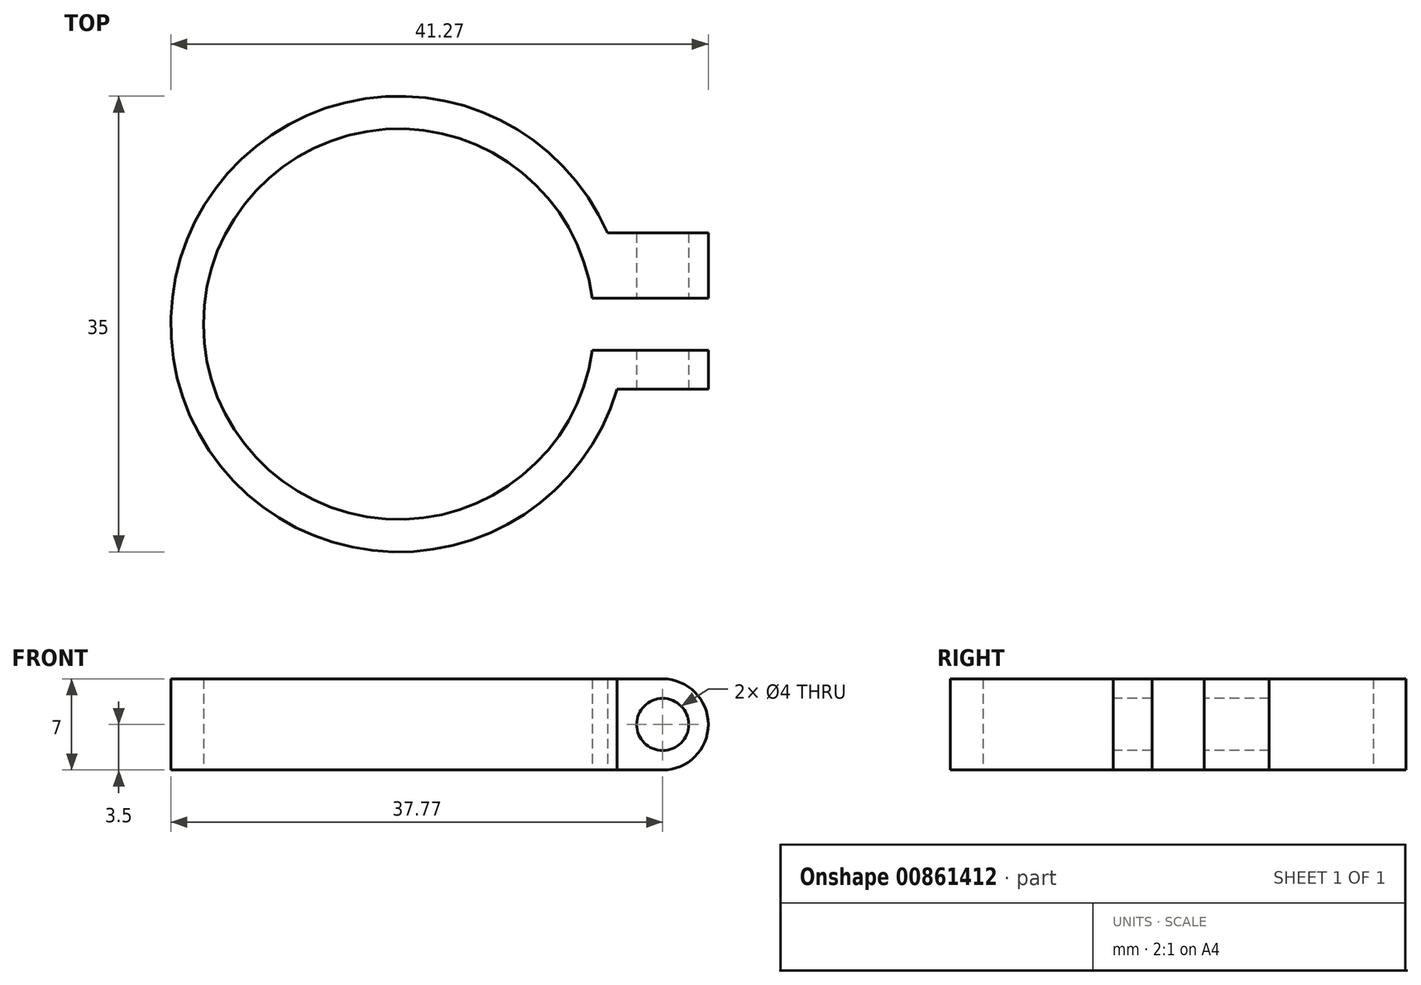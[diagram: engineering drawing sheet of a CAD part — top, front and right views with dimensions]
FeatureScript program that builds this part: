
annotation { "Feature Type Name" : "Feature", "Feature Type Description" : "" }
export const myFeature = defineFeature(function(context is Context, id is Id, definition is map)
    precondition{}
    {
        {
            var Q0;
            Q0=qCreatedBy(makeId("Top.planeOp"),FACE);
            var sketch = newSketch(context, id + "F0", { "sketchPlane" : qUnion([Q0])});
            skCircle(sketch, "E0", {"center": v(0, 0) * mm, "radius": 15 * mm});
            skCircle(sketch, "E1", {"center": v(0, 0) * mm, "radius": 17.5 * mm});
            skLineSegment(sketch, "E2", {"start": v(0, 0) * mm, "end": v(30.45, 0) * mm});
            skLineSegment(sketch, "E3.0", {"start": v(0, -2) * mm, "end": v(30.45, -2) * mm});
            skLineSegment(sketch, "E4.0", {"start": v(0, 2) * mm, "end": v(30.45, 2) * mm});
            skLineSegment(sketch, "E5.bottom", {"start": v(16.77, 5) * mm, "end": v(23.77, 5) * mm});
            skLineSegment(sketch, "E5.top", {"start": v(16.77, -5) * mm, "end": v(23.77, -5) * mm});
            skLineSegment(sketch, "E5.left", {"start": v(16.77, 5) * mm, "end": v(16.77, -5) * mm});
            skLineSegment(sketch, "E5.right", {"start": v(23.77, 5) * mm, "end": v(23.77, -5) * mm});
            skLineSegment(sketch, "E6.top", {"start": v(16.77, 7) * mm, "end": v(23.77, 7) * mm});
            skLineSegment(sketch, "E6.left", {"start": v(16.77, 5) * mm, "end": v(16.77, 7) * mm});
            skLineSegment(sketch, "E6.right", {"start": v(23.77, 5) * mm, "end": v(23.77, 7) * mm});
            skLineSegment(sketch, "E7.bottom", {"start": v(16.77, 5) * mm, "end": v(16.04, 5) * mm});
            skLineSegment(sketch, "E7.top", {"start": v(16.77, 7) * mm, "end": v(16.04, 7) * mm});
            skLineSegment(sketch, "E7.right", {"start": v(16.04, 5) * mm, "end": v(16.04, 7) * mm});
            skSolve(sketch);
        }
        {
            var Q0;
            {var subQ0=sQuery(id+"F0.wireOp",EDGE,"E4.0");var subQ1=sQuery(id+"F0.wireOp",EDGE,"E0");var subQ2=makeQuery(id+"F0.imprint","INTERSECT",VERTEX,{"derivedFrom":[subQ1,subQ0]});Q0=makeQuery(id+"F0.imprint","IMPRINT",FACE,{"disambiguationData":[TD([[makeQuery(id+"F0.imprint","IMPRINT",EDGE,{"disambiguationData":[TD([[subQ2,-1.0]])],"derivedFrom":subQ1}),-1.0]])]});}
            var Q1;
            {var subQ1=sQuery(id+"F0.wireOp",EDGE,"E1");var subQ3=sQuery(id+"F0.wireOp",EDGE,"E4.0");var subQ4=makeQuery(id+"F0.imprint","INTERSECT",VERTEX,{"derivedFrom":[subQ1,subQ3]});Q1=makeQuery(id+"F0.imprint","IMPRINT",FACE,{"disambiguationData":[TD([[makeQuery(id+"F0.imprint","IMPRINT",EDGE,{"disambiguationData":[TD([[subQ4,1.0]])],"derivedFrom":subQ3}),1.0]])]});}
            var Q2;
            {var subQ0=sQuery(id+"F0.wireOp",EDGE,"E5.bottom");Q2=makeQuery(id+"F0.imprint","IMPRINT",FACE,{"disambiguationData":[TD([[makeQuery(id+"F0.imprint","IMPRINT",EDGE,{"derivedFrom":subQ0}),-1.0]])]});}
            var Q3;
            {var subQ0=sQuery(id+"F0.wireOp",EDGE,"E5.top");Q3=makeQuery(id+"F0.imprint","IMPRINT",FACE,{"disambiguationData":[TD([[makeQuery(id+"F0.imprint","IMPRINT",EDGE,{"derivedFrom":subQ0}),1.0]])]});}
            var Q4;
            {var subQ1=sQuery(id+"F0.wireOp",EDGE,"E1");var subQ3=sQuery(id+"F0.wireOp",EDGE,"E3.0");var subQ4=makeQuery(id+"F0.imprint","INTERSECT",VERTEX,{"derivedFrom":[subQ1,subQ3]});Q4=makeQuery(id+"F0.imprint","IMPRINT",FACE,{"disambiguationData":[TD([[makeQuery(id+"F0.imprint","IMPRINT",EDGE,{"disambiguationData":[TD([[subQ4,1.0]])],"derivedFrom":subQ3}),-1.0]])]});}
            var Q5;
            {var subQ0=sQuery(id+"F0.wireOp",EDGE,"E5.bottom");Q5=makeQuery(id+"F0.imprint","IMPRINT",FACE,{"disambiguationData":[TD([[makeQuery(id+"F0.imprint","IMPRINT",EDGE,{"derivedFrom":subQ0}),-1.0]])]});}
            var Q6;
            Q6=makeQuery(id+"F0.imprint","IMPRINT",FACE,{"disambiguationData":[TD([[makeQuery(id+"F0.imprint","IMPRINT",EDGE,{"derivedFrom":sQuery(id+"F0.wireOp",EDGE,"E5.bottom")}),1.0]])]});
            var Q7;
            {var subQ0=sQuery(id+"F0.wireOp",EDGE,"E7.bottom");Q7=makeQuery(id+"F0.imprint","IMPRINT",FACE,{"disambiguationData":[TD([[makeQuery(id+"F0.imprint","IMPRINT",EDGE,{"derivedFrom":subQ0}),-1.0]])]});}
            var Q8;
            {var subQ2=sQuery(id+"F0.wireOp",EDGE,"E7.top");Q8=makeQuery(id+"F0.imprint","IMPRINT",FACE,{"disambiguationData":[TD([[makeQuery(id+"F0.imprint","IMPRINT",EDGE,{"derivedFrom":subQ2}),1.0]])]});}
            extrude(context, id + "F1", {"entities" : qUnion([Q0, Q1, Q2, Q3, Q4, Q5, Q6, Q7, Q8]), "depth" : 7 * mm, "offsetDistance" : 25 * mm});
        }
        {
            var Q0;
            Q0=makeQuery(id+"F1.opExtrude","SWEPT_FACE",FACE,{"disambiguationData":[OSD([sQuery(id+"F0.wireOp",EDGE,"E5.top")])]});
            var sketch = newSketch(context, id + "F2", { "sketchPlane" : qUnion([Q0])});
            skCircle(sketch, "E8", {"center": v(20.27, 3.5) * mm, "radius": 2 * mm});
            skPoint(sketch, "E9", {"position": v(20.27, 7) * mm});
            skPoint(sketch, "E10", {"position": v(23.77, 3.5) * mm});
            skSolve(sketch);
        }
        {
            var Q0;
            Q0=qSketchRegion(id+"F2",true);
            extrude(context, id + "F3", {"entities" : qUnion([Q0]), "operationType" : NewBodyOperationType.REMOVE, "oppositeDirection" : true, "depth" : 25 * mm, "offsetDistance" : 25 * mm});
        }
        {
            var Q0;
            {var subQ0=sQuery(id+"F0.wireOp",EDGE,"E5.right");Q0=makeQuery(id+"F1.opExtrude","CAP_EDGE",EDGE,{"disambiguationData":[OSD([subQ0]),TDD([makeQuery(id+"F0.imprint","IMPRINT",EDGE,{"disambiguationData":[TD([[makeQuery(id+"F0.imprint","INTERSECT",VERTEX,{"derivedFrom":[sQuery(id+"F0.wireOp",EDGE,"E5.top"),subQ0]}),1.0]])],"derivedFrom":subQ0})])],"isStart":false});}
            var Q1;
            {var subQ0=sQuery(id+"F0.wireOp",EDGE,"E5.right");Q1=makeQuery(id+"F1.opExtrude","CAP_EDGE",EDGE,{"disambiguationData":[OSD([subQ0]),TDD([makeQuery(id+"F0.imprint","IMPRINT",EDGE,{"disambiguationData":[TD([[makeQuery(id+"F0.imprint","INTERSECT",VERTEX,{"derivedFrom":[sQuery(id+"F0.wireOp",EDGE,"E5.bottom"),subQ0]}),-1.0]])],"derivedFrom":subQ0})])],"isStart":false});}
            var Q2;
            {var subQ0=sQuery(id+"F0.wireOp",EDGE,"E5.right");Q2=makeQuery(id+"F1.opExtrude","CAP_EDGE",EDGE,{"disambiguationData":[OSD([subQ0]),TDD([makeQuery(id+"F0.imprint","IMPRINT",EDGE,{"disambiguationData":[TD([[makeQuery(id+"F0.imprint","INTERSECT",VERTEX,{"derivedFrom":[sQuery(id+"F0.wireOp",EDGE,"E5.top"),subQ0]}),1.0]])],"derivedFrom":subQ0})])],"isStart":true});}
            var Q3;
            {var subQ0=sQuery(id+"F0.wireOp",EDGE,"E5.right");Q3=makeQuery(id+"F1.opExtrude","CAP_EDGE",EDGE,{"disambiguationData":[OSD([subQ0]),TDD([makeQuery(id+"F0.imprint","IMPRINT",EDGE,{"disambiguationData":[TD([[makeQuery(id+"F0.imprint","INTERSECT",VERTEX,{"derivedFrom":[sQuery(id+"F0.wireOp",EDGE,"E5.bottom"),subQ0]}),-1.0]])],"derivedFrom":subQ0})])],"isStart":true});}
            var Q4;
            Q4=makeQuery(id+"F1.opExtrude","CAP_EDGE",EDGE,{"disambiguationData":[OSD([sQuery(id+"F0.wireOp",EDGE,"E5.right"),sQuery(id+"F0.wireOp",EDGE,"E6.right")])],"isStart":true});
            var Q5;
            Q5=makeQuery(id+"F1.opExtrude","CAP_EDGE",EDGE,{"disambiguationData":[OSD([sQuery(id+"F0.wireOp",EDGE,"E5.right"),sQuery(id+"F0.wireOp",EDGE,"E6.right")])],"isStart":false});
            fillet(context, id + "F4", {"entities" : qUnion([Q0, Q1, Q2, Q3, Q4, Q5]), "radius" : 3.5 * mm, "tangentPropagation" : true, "allowEdgeOverflow" : false});
        }
    });
